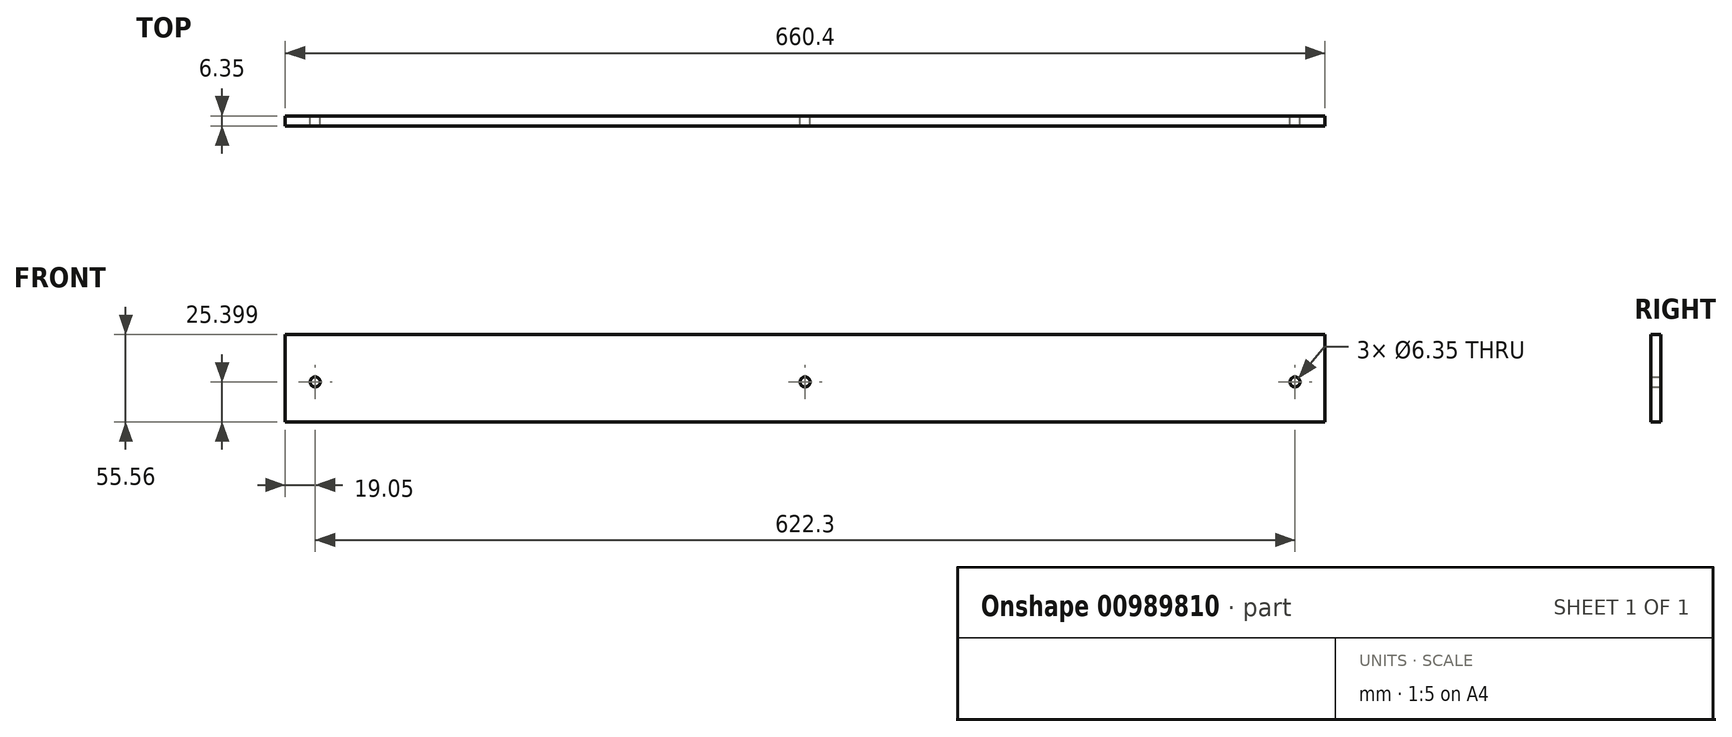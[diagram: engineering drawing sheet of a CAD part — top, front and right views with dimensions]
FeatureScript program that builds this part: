
annotation { "Feature Type Name" : "Feature", "Feature Type Description" : "" }
export const myFeature = defineFeature(function(context is Context, id is Id, definition is map)
    precondition{}
    {
        {
            var Q0;
            Q0=qCreatedBy(makeId("Front.planeOp"),FACE);
            var sketch = newSketch(context, id + "F0", { "sketchPlane" : qUnion([Q0])});
            skLineSegment(sketch, "E0.bottom", {"start": v(-330.2, 27.78) * mm, "end": v(330.2, 27.78) * mm});
            skLineSegment(sketch, "E0.top", {"start": v(-330.2, -27.78) * mm, "end": v(330.2, -27.78) * mm});
            skLineSegment(sketch, "E0.left", {"start": v(-330.2, 27.78) * mm, "end": v(-330.2, -27.78) * mm});
            skLineSegment(sketch, "E0.right", {"start": v(330.2, 27.78) * mm, "end": v(330.2, -27.78) * mm});
            skCircle(sketch, "E1", {"center": v(-311.15, -2.38) * mm, "radius": 3.18 * mm});
            skCircle(sketch, "E2.1.0.0", {"center": v(0, -2.38) * mm, "radius": 3.18 * mm});
            skCircle(sketch, "E2.2.0.0", {"center": v(311.15, -2.38) * mm, "radius": 3.18 * mm});
            skLineSegment(sketch, "E2.direction1", {"start": v(-311.15, -2.38) * mm, "end": v(0, -2.38) * mm, "construction": true});
            skSolve(sketch);
        }
        {
            var Q0;
            Q0=makeQuery(id+"F0.imprint","IMPRINT",FACE,{"disambiguationData":[TD([[makeQuery(id+"F0.imprint","IMPRINT",EDGE,{"derivedFrom":sQuery(id+"F0.wireOp",EDGE,"E0.bottom")}),-1.0]])]});
            extrude(context, id + "F1", {"entities" : qUnion([Q0]), "depth" : 6.35 * mm, "offsetDistance" : 25.4 * mm});
        }
    });
